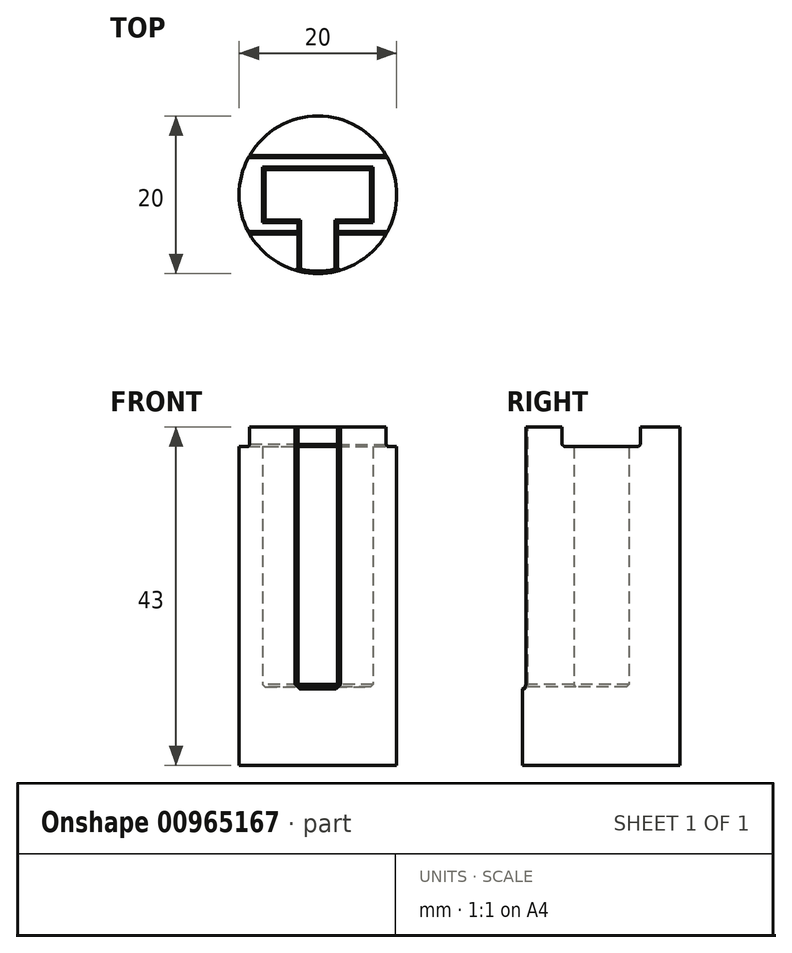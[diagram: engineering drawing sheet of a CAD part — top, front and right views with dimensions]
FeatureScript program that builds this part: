
annotation { "Feature Type Name" : "Feature", "Feature Type Description" : "" }
export const myFeature = defineFeature(function(context is Context, id is Id, definition is map)
    precondition{}
    {
        {
            var Q0;
            Q0=qCreatedBy(makeId("Top.planeOp"),FACE);
            var sketch = newSketch(context, id + "F0", { "sketchPlane" : qUnion([Q0])});
            skCircle(sketch, "E0", {"center": v(0, 0) * mm, "radius": 10 * mm});
            skLineSegment(sketch, "E1.bottom", {"start": v(7, 3.5) * mm, "end": v(-7, 3.5) * mm});
            skLineSegment(sketch, "E1.top", {"start": v(7, -3.5) * mm, "end": v(-7, -3.5) * mm});
            skLineSegment(sketch, "E1.left", {"start": v(7, 3.5) * mm, "end": v(7, -3.5) * mm});
            skLineSegment(sketch, "E1.right", {"start": v(-7, 3.5) * mm, "end": v(-7, -3.5) * mm});
            skLineSegment(sketch, "E2", {"start": v(0, 0) * mm, "end": v(0, -15.29) * mm, "construction": true});
            skLineSegment(sketch, "E3.bottom", {"start": v(2.5, -11.79) * mm, "end": v(-2.5, -11.79) * mm});
            skLineSegment(sketch, "E3.top", {"start": v(2.5, -3.5) * mm, "end": v(-2.5, -3.5) * mm});
            skLineSegment(sketch, "E3.left", {"start": v(2.5, -11.79) * mm, "end": v(2.5, -3.5) * mm});
            skLineSegment(sketch, "E3.right", {"start": v(-2.5, -11.79) * mm, "end": v(-2.5, -3.5) * mm});
            skPoint(sketch, "E3.middle", {"position": v(0, -7.64) * mm});
            skSolve(sketch);
        }
        {
            var Q0;
            Q0=makeQuery(id+"F0.imprint","IMPRINT",FACE,{"disambiguationData":[TD([[makeQuery(id+"F0.imprint","IMPRINT",EDGE,{"derivedFrom":sQuery(id+"F0.wireOp",EDGE,"E1.bottom")}),-1.0]])]});
            extrude(context, id + "F1", {"entities" : qUnion([Q0]), "depth" : 43 * mm, "offsetDistance" : 25 * mm});
        }
        {
            var Q0;
            Q0=makeQuery(id+"F0.imprint","IMPRINT",FACE,{"disambiguationData":[TD([[makeQuery(id+"F0.imprint","IMPRINT",EDGE,{"derivedFrom":sQuery(id+"F0.wireOp",EDGE,"E1.bottom")}),1.0]])]});
            var Q1;
            {var subQ0=sQuery(id+"F0.wireOp",EDGE,"E3.left");var subQ1=sQuery(id+"F0.wireOp",EDGE,"E0");var subQ2=makeQuery(id+"F0.imprint","INTERSECT",VERTEX,{"derivedFrom":[subQ1,subQ0]});Q1=makeQuery(id+"F0.imprint","IMPRINT",FACE,{"disambiguationData":[TD([[makeQuery(id+"F0.imprint","IMPRINT",EDGE,{"disambiguationData":[TD([[subQ2,1.0]])],"derivedFrom":subQ1}),1.0]])]});}
            extrude(context, id + "F2", {"entities" : qUnion([Q0, Q1]), "operationType" : NewBodyOperationType.ADD, "depth" : 10 * mm, "offsetDistance" : 25 * mm});
        }
        {
            var Q0;
            Q0=qCreatedBy(makeId("Right.planeOp"),FACE);
            var sketch = newSketch(context, id + "F3", { "sketchPlane" : qUnion([Q0])});
            skLineSegment(sketch, "E4.bottom", {"start": v(-5, 40.5) * mm, "end": v(5, 40.5) * mm});
            skLineSegment(sketch, "E4.top", {"start": v(-5, 45.5) * mm, "end": v(5, 45.5) * mm});
            skLineSegment(sketch, "E4.left", {"start": v(-5, 40.5) * mm, "end": v(-5, 45.5) * mm});
            skLineSegment(sketch, "E4.right", {"start": v(5, 40.5) * mm, "end": v(5, 45.5) * mm});
            skPoint(sketch, "E4.middle", {"position": v(0, 43) * mm});
            skSolve(sketch);
        }
        {
            var Q0;
            Q0 = qSketchRegion(id + "F3", true);
            extrude(context, id + "F4", {"entities" : qUnion([Q0]), "operationType" : NewBodyOperationType.REMOVE, "endBound" : BoundingType.SYMMETRIC, "oppositeDirection" : true, "depth" : 25 * mm, "offsetDistance" : 25 * mm});
        }
        {
            var Q0;
            Q0=makeQuery(id+"F4.boolean.opBoolean","COPY",EDGE,{"derivedFrom":makeQuery(id+"F4.opExtrude","SWEPT_EDGE",EDGE,{"disambiguationData":[OSD([sQuery(id+"F3.wireOp",EDGE,"E4.bottom"),sQuery(id+"F3.wireOp",EDGE,"E4.right")])]})});
            var Q1;
            {var subQ1=sQuery(id+"F3.wireOp",EDGE,"E4.bottom");var subQ2=sQuery(id+"F3.wireOp",EDGE,"E4.left");Q1=makeQuery(id+"F4.boolean.opBoolean","COPY",EDGE,{"disambiguationData":[TD([makeQuery(id+"F1.opExtrude","SWEPT_FACE",FACE,{"disambiguationData":[OSD([sQuery(id+"F0.wireOp",EDGE,"E3.right")])]})])],"derivedFrom":makeQuery(id+"F4.opExtrude","SWEPT_EDGE",EDGE,{"disambiguationData":[OSD([subQ1,subQ2])]})});}
            var Q2;
            {var subQ1=sQuery(id+"F3.wireOp",EDGE,"E4.bottom");var subQ2=sQuery(id+"F3.wireOp",EDGE,"E4.left");Q2=makeQuery(id+"F4.boolean.opBoolean","COPY",EDGE,{"disambiguationData":[TD([makeQuery(id+"F1.opExtrude","SWEPT_FACE",FACE,{"disambiguationData":[OSD([sQuery(id+"F0.wireOp",EDGE,"E3.left")])]})])],"derivedFrom":makeQuery(id+"F4.opExtrude","SWEPT_EDGE",EDGE,{"disambiguationData":[OSD([subQ1,subQ2])]})});}
            chamfer(context, id + "F5", {"entities" : qUnion([Q0, Q1, Q2]), "width" : 0.3 * mm, "tangentPropagation" : true});
        }
        {
            var Q0;
            Q0=makeQuery(id+"F2.opExtrude","CAP_EDGE",EDGE,{"disambiguationData":[OSD([sQuery(id+"F0.wireOp",EDGE,"E0")])],"isStart":false});
            var Q1;
            {var subQ0=sQuery(id+"F0.wireOp",EDGE,"E1.top");Q1=makeQuery(id+"F2.opExtrude","CAP_EDGE",EDGE,{"disambiguationData":[OSD([subQ0]),TDD([makeQuery(id+"F0.imprint","IMPRINT",EDGE,{"disambiguationData":[TD([[makeQuery(id+"F0.imprint","INTERSECT",VERTEX,{"derivedFrom":[subQ0,sQuery(id+"F0.wireOp",EDGE,"E3.left")]}),1.0]])],"derivedFrom":subQ0})])],"isStart":false});}
            var Q2;
            Q2=makeQuery(id+"F2.opExtrude","CAP_EDGE",EDGE,{"disambiguationData":[OSD([sQuery(id+"F0.wireOp",EDGE,"E1.left")])],"isStart":false});
            var Q3;
            Q3=makeQuery(id+"F2.opExtrude","CAP_FACE",FACE,{"disambiguationData":[OSD([sQuery(id+"F0.wireOp",EDGE,"E0"),sQuery(id+"F0.wireOp",EDGE,"E1.bottom"),sQuery(id+"F0.wireOp",EDGE,"E1.top"),sQuery(id+"F0.wireOp",EDGE,"E1.left"),sQuery(id+"F0.wireOp",EDGE,"E1.right"),sQuery(id+"F0.wireOp",EDGE,"E3.left"),sQuery(id+"F0.wireOp",EDGE,"E3.right")])],"isStart":false});
            var Q4;
            Q4=makeQuery(id+"F2.opExtrude","CAP_EDGE",EDGE,{"disambiguationData":[OSD([sQuery(id+"F0.wireOp",EDGE,"E1.right")])],"isStart":false});
            chamfer(context, id + "F6", {"entities" : qUnion([Q0, Q1, Q2, Q3, Q4]), "width" : 0.3 * mm, "tangentPropagation" : true});
        }
    });
